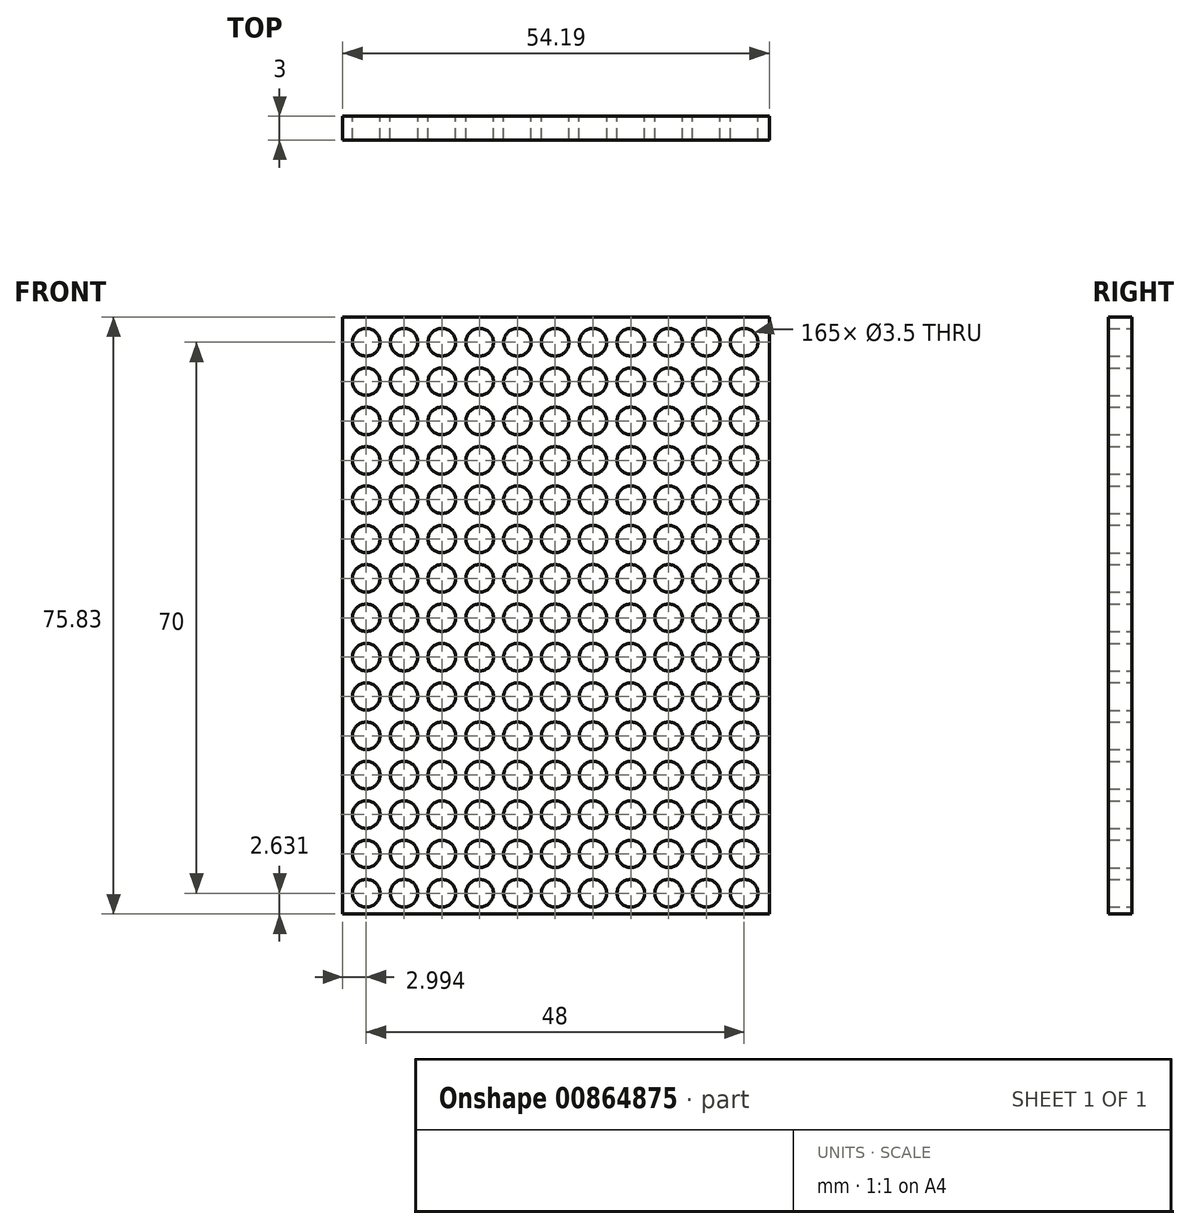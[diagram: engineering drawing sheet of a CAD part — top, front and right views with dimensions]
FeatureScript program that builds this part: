
annotation { "Feature Type Name" : "Feature", "Feature Type Description" : "" }
export const myFeature = defineFeature(function(context is Context, id is Id, definition is map)
    precondition{}
    {
        {
            var Q0;
            Q0=qCreatedBy(makeId("Front.planeOp"),FACE);
            var sketch = newSketch(context, id + "F0", { "sketchPlane" : qUnion([Q0])});
            skCircle(sketch, "E0", {"center": v(3, 2.63) * mm, "radius": 1.75 * mm});
            skCircle(sketch, "E1.0.1.0", {"center": v(3, 7.63) * mm, "radius": 1.75 * mm});
            skCircle(sketch, "E1.0.2.0", {"center": v(3, 12.63) * mm, "radius": 1.75 * mm});
            skCircle(sketch, "E1.0.3.0", {"center": v(3, 17.63) * mm, "radius": 1.75 * mm});
            skCircle(sketch, "E1.0.4.0", {"center": v(3, 22.63) * mm, "radius": 1.75 * mm});
            skCircle(sketch, "E1.0.5.0", {"center": v(3, 27.63) * mm, "radius": 1.75 * mm});
            skCircle(sketch, "E1.0.6.0", {"center": v(3, 32.63) * mm, "radius": 1.75 * mm});
            skCircle(sketch, "E1.0.7.0", {"center": v(3, 37.63) * mm, "radius": 1.75 * mm});
            skCircle(sketch, "E1.0.8.0", {"center": v(3, 42.63) * mm, "radius": 1.75 * mm});
            skCircle(sketch, "E1.0.9.0", {"center": v(3, 47.63) * mm, "radius": 1.75 * mm});
            skCircle(sketch, "E1.0.10.0", {"center": v(3, 52.63) * mm, "radius": 1.75 * mm});
            skCircle(sketch, "E1.0.11.0", {"center": v(3, 57.63) * mm, "radius": 1.75 * mm});
            skCircle(sketch, "E1.0.12.0", {"center": v(3, 62.63) * mm, "radius": 1.75 * mm});
            skCircle(sketch, "E1.0.13.0", {"center": v(3, 67.63) * mm, "radius": 1.75 * mm});
            skCircle(sketch, "E1.0.14.0", {"center": v(3, 72.63) * mm, "radius": 1.75 * mm});
            skCircle(sketch, "E1.1.0.0", {"center": v(7.8, 2.63) * mm, "radius": 1.75 * mm});
            skCircle(sketch, "E1.1.1.0", {"center": v(7.8, 7.63) * mm, "radius": 1.75 * mm});
            skCircle(sketch, "E1.1.2.0", {"center": v(7.8, 12.63) * mm, "radius": 1.75 * mm});
            skCircle(sketch, "E1.1.3.0", {"center": v(7.8, 17.63) * mm, "radius": 1.75 * mm});
            skCircle(sketch, "E1.1.4.0", {"center": v(7.8, 22.63) * mm, "radius": 1.75 * mm});
            skCircle(sketch, "E1.1.5.0", {"center": v(7.8, 27.63) * mm, "radius": 1.75 * mm});
            skCircle(sketch, "E1.1.6.0", {"center": v(7.8, 32.63) * mm, "radius": 1.75 * mm});
            skCircle(sketch, "E1.1.7.0", {"center": v(7.8, 37.63) * mm, "radius": 1.75 * mm});
            skCircle(sketch, "E1.1.8.0", {"center": v(7.8, 42.63) * mm, "radius": 1.75 * mm});
            skCircle(sketch, "E1.1.9.0", {"center": v(7.8, 47.63) * mm, "radius": 1.75 * mm});
            skCircle(sketch, "E1.1.10.0", {"center": v(7.8, 52.63) * mm, "radius": 1.75 * mm});
            skCircle(sketch, "E1.1.11.0", {"center": v(7.8, 57.63) * mm, "radius": 1.75 * mm});
            skCircle(sketch, "E1.1.12.0", {"center": v(7.8, 62.63) * mm, "radius": 1.75 * mm});
            skCircle(sketch, "E1.1.13.0", {"center": v(7.8, 67.63) * mm, "radius": 1.75 * mm});
            skCircle(sketch, "E1.1.14.0", {"center": v(7.8, 72.63) * mm, "radius": 1.75 * mm});
            skCircle(sketch, "E1.2.0.0", {"center": v(12.6, 2.63) * mm, "radius": 1.75 * mm});
            skCircle(sketch, "E1.2.1.0", {"center": v(12.6, 7.63) * mm, "radius": 1.75 * mm});
            skCircle(sketch, "E1.2.2.0", {"center": v(12.6, 12.63) * mm, "radius": 1.75 * mm});
            skCircle(sketch, "E1.2.3.0", {"center": v(12.6, 17.63) * mm, "radius": 1.75 * mm});
            skCircle(sketch, "E1.2.4.0", {"center": v(12.6, 22.63) * mm, "radius": 1.75 * mm});
            skCircle(sketch, "E1.2.5.0", {"center": v(12.6, 27.63) * mm, "radius": 1.75 * mm});
            skCircle(sketch, "E1.2.6.0", {"center": v(12.6, 32.63) * mm, "radius": 1.75 * mm});
            skCircle(sketch, "E1.2.7.0", {"center": v(12.6, 37.63) * mm, "radius": 1.75 * mm});
            skCircle(sketch, "E1.2.8.0", {"center": v(12.6, 42.63) * mm, "radius": 1.75 * mm});
            skCircle(sketch, "E1.2.9.0", {"center": v(12.6, 47.63) * mm, "radius": 1.75 * mm});
            skCircle(sketch, "E1.2.10.0", {"center": v(12.6, 52.63) * mm, "radius": 1.75 * mm});
            skCircle(sketch, "E1.2.11.0", {"center": v(12.6, 57.63) * mm, "radius": 1.75 * mm});
            skCircle(sketch, "E1.2.12.0", {"center": v(12.6, 62.63) * mm, "radius": 1.75 * mm});
            skCircle(sketch, "E1.2.13.0", {"center": v(12.6, 67.63) * mm, "radius": 1.75 * mm});
            skCircle(sketch, "E1.2.14.0", {"center": v(12.6, 72.63) * mm, "radius": 1.75 * mm});
            skCircle(sketch, "E1.3.0.0", {"center": v(17.4, 2.63) * mm, "radius": 1.75 * mm});
            skCircle(sketch, "E1.3.1.0", {"center": v(17.4, 7.63) * mm, "radius": 1.75 * mm});
            skCircle(sketch, "E1.3.2.0", {"center": v(17.4, 12.63) * mm, "radius": 1.75 * mm});
            skCircle(sketch, "E1.3.3.0", {"center": v(17.4, 17.63) * mm, "radius": 1.75 * mm});
            skCircle(sketch, "E1.3.4.0", {"center": v(17.4, 22.63) * mm, "radius": 1.75 * mm});
            skCircle(sketch, "E1.3.5.0", {"center": v(17.4, 27.63) * mm, "radius": 1.75 * mm});
            skCircle(sketch, "E1.3.6.0", {"center": v(17.4, 32.63) * mm, "radius": 1.75 * mm});
            skCircle(sketch, "E1.3.7.0", {"center": v(17.4, 37.63) * mm, "radius": 1.75 * mm});
            skCircle(sketch, "E1.3.8.0", {"center": v(17.4, 42.63) * mm, "radius": 1.75 * mm});
            skCircle(sketch, "E1.3.9.0", {"center": v(17.4, 47.63) * mm, "radius": 1.75 * mm});
            skCircle(sketch, "E1.3.10.0", {"center": v(17.4, 52.63) * mm, "radius": 1.75 * mm});
            skCircle(sketch, "E1.3.11.0", {"center": v(17.4, 57.63) * mm, "radius": 1.75 * mm});
            skCircle(sketch, "E1.3.12.0", {"center": v(17.4, 62.63) * mm, "radius": 1.75 * mm});
            skCircle(sketch, "E1.3.13.0", {"center": v(17.4, 67.63) * mm, "radius": 1.75 * mm});
            skCircle(sketch, "E1.3.14.0", {"center": v(17.4, 72.63) * mm, "radius": 1.75 * mm});
            skCircle(sketch, "E1.4.0.0", {"center": v(22.2, 2.63) * mm, "radius": 1.75 * mm});
            skCircle(sketch, "E1.4.1.0", {"center": v(22.2, 7.63) * mm, "radius": 1.75 * mm});
            skCircle(sketch, "E1.4.2.0", {"center": v(22.2, 12.63) * mm, "radius": 1.75 * mm});
            skCircle(sketch, "E1.4.3.0", {"center": v(22.2, 17.63) * mm, "radius": 1.75 * mm});
            skCircle(sketch, "E1.4.4.0", {"center": v(22.2, 22.63) * mm, "radius": 1.75 * mm});
            skCircle(sketch, "E1.4.5.0", {"center": v(22.2, 27.63) * mm, "radius": 1.75 * mm});
            skCircle(sketch, "E1.4.6.0", {"center": v(22.2, 32.63) * mm, "radius": 1.75 * mm});
            skCircle(sketch, "E1.4.7.0", {"center": v(22.2, 37.63) * mm, "radius": 1.75 * mm});
            skCircle(sketch, "E1.4.8.0", {"center": v(22.2, 42.63) * mm, "radius": 1.75 * mm});
            skCircle(sketch, "E1.4.9.0", {"center": v(22.2, 47.63) * mm, "radius": 1.75 * mm});
            skCircle(sketch, "E1.4.10.0", {"center": v(22.2, 52.63) * mm, "radius": 1.75 * mm});
            skCircle(sketch, "E1.4.11.0", {"center": v(22.2, 57.63) * mm, "radius": 1.75 * mm});
            skCircle(sketch, "E1.4.12.0", {"center": v(22.2, 62.63) * mm, "radius": 1.75 * mm});
            skCircle(sketch, "E1.4.13.0", {"center": v(22.2, 67.63) * mm, "radius": 1.75 * mm});
            skCircle(sketch, "E1.4.14.0", {"center": v(22.2, 72.63) * mm, "radius": 1.75 * mm});
            skCircle(sketch, "E1.5.0.0", {"center": v(27, 2.63) * mm, "radius": 1.75 * mm});
            skCircle(sketch, "E1.5.1.0", {"center": v(27, 7.63) * mm, "radius": 1.75 * mm});
            skCircle(sketch, "E1.5.2.0", {"center": v(27, 12.63) * mm, "radius": 1.75 * mm});
            skCircle(sketch, "E1.5.3.0", {"center": v(27, 17.63) * mm, "radius": 1.75 * mm});
            skCircle(sketch, "E1.5.4.0", {"center": v(27, 22.63) * mm, "radius": 1.75 * mm});
            skCircle(sketch, "E1.5.5.0", {"center": v(27, 27.63) * mm, "radius": 1.75 * mm});
            skCircle(sketch, "E1.5.6.0", {"center": v(27, 32.63) * mm, "radius": 1.75 * mm});
            skCircle(sketch, "E1.5.7.0", {"center": v(27, 37.63) * mm, "radius": 1.75 * mm});
            skCircle(sketch, "E1.5.8.0", {"center": v(27, 42.63) * mm, "radius": 1.75 * mm});
            skCircle(sketch, "E1.5.9.0", {"center": v(27, 47.63) * mm, "radius": 1.75 * mm});
            skCircle(sketch, "E1.5.10.0", {"center": v(27, 52.63) * mm, "radius": 1.75 * mm});
            skCircle(sketch, "E1.5.11.0", {"center": v(27, 57.63) * mm, "radius": 1.75 * mm});
            skCircle(sketch, "E1.5.12.0", {"center": v(27, 62.63) * mm, "radius": 1.75 * mm});
            skCircle(sketch, "E1.5.13.0", {"center": v(27, 67.63) * mm, "radius": 1.75 * mm});
            skCircle(sketch, "E1.5.14.0", {"center": v(27, 72.63) * mm, "radius": 1.75 * mm});
            skCircle(sketch, "E1.6.0.0", {"center": v(31.8, 2.63) * mm, "radius": 1.75 * mm});
            skCircle(sketch, "E1.6.1.0", {"center": v(31.8, 7.63) * mm, "radius": 1.75 * mm});
            skCircle(sketch, "E1.6.2.0", {"center": v(31.8, 12.63) * mm, "radius": 1.75 * mm});
            skCircle(sketch, "E1.6.3.0", {"center": v(31.8, 17.63) * mm, "radius": 1.75 * mm});
            skCircle(sketch, "E1.6.4.0", {"center": v(31.8, 22.63) * mm, "radius": 1.75 * mm});
            skCircle(sketch, "E1.6.5.0", {"center": v(31.8, 27.63) * mm, "radius": 1.75 * mm});
            skCircle(sketch, "E1.6.6.0", {"center": v(31.8, 32.63) * mm, "radius": 1.75 * mm});
            skCircle(sketch, "E1.6.7.0", {"center": v(31.8, 37.63) * mm, "radius": 1.75 * mm});
            skCircle(sketch, "E1.6.8.0", {"center": v(31.8, 42.63) * mm, "radius": 1.75 * mm});
            skCircle(sketch, "E1.6.9.0", {"center": v(31.8, 47.63) * mm, "radius": 1.75 * mm});
            skCircle(sketch, "E1.6.10.0", {"center": v(31.8, 52.63) * mm, "radius": 1.75 * mm});
            skCircle(sketch, "E1.6.11.0", {"center": v(31.8, 57.63) * mm, "radius": 1.75 * mm});
            skCircle(sketch, "E1.6.12.0", {"center": v(31.8, 62.63) * mm, "radius": 1.75 * mm});
            skCircle(sketch, "E1.6.13.0", {"center": v(31.8, 67.63) * mm, "radius": 1.75 * mm});
            skCircle(sketch, "E1.6.14.0", {"center": v(31.8, 72.63) * mm, "radius": 1.75 * mm});
            skCircle(sketch, "E1.7.0.0", {"center": v(36.6, 2.63) * mm, "radius": 1.75 * mm});
            skCircle(sketch, "E1.7.1.0", {"center": v(36.6, 7.63) * mm, "radius": 1.75 * mm});
            skCircle(sketch, "E1.7.2.0", {"center": v(36.6, 12.63) * mm, "radius": 1.75 * mm});
            skCircle(sketch, "E1.7.3.0", {"center": v(36.6, 17.63) * mm, "radius": 1.75 * mm});
            skCircle(sketch, "E1.7.4.0", {"center": v(36.6, 22.63) * mm, "radius": 1.75 * mm});
            skCircle(sketch, "E1.7.5.0", {"center": v(36.6, 27.63) * mm, "radius": 1.75 * mm});
            skCircle(sketch, "E1.7.6.0", {"center": v(36.6, 32.63) * mm, "radius": 1.75 * mm});
            skCircle(sketch, "E1.7.7.0", {"center": v(36.6, 37.63) * mm, "radius": 1.75 * mm});
            skCircle(sketch, "E1.7.8.0", {"center": v(36.6, 42.63) * mm, "radius": 1.75 * mm});
            skCircle(sketch, "E1.7.9.0", {"center": v(36.6, 47.63) * mm, "radius": 1.75 * mm});
            skCircle(sketch, "E1.7.10.0", {"center": v(36.6, 52.63) * mm, "radius": 1.75 * mm});
            skCircle(sketch, "E1.7.11.0", {"center": v(36.6, 57.63) * mm, "radius": 1.75 * mm});
            skCircle(sketch, "E1.7.12.0", {"center": v(36.6, 62.63) * mm, "radius": 1.75 * mm});
            skCircle(sketch, "E1.7.13.0", {"center": v(36.6, 67.63) * mm, "radius": 1.75 * mm});
            skCircle(sketch, "E1.7.14.0", {"center": v(36.6, 72.63) * mm, "radius": 1.75 * mm});
            skCircle(sketch, "E1.8.0.0", {"center": v(41.4, 2.63) * mm, "radius": 1.75 * mm});
            skCircle(sketch, "E1.8.1.0", {"center": v(41.4, 7.63) * mm, "radius": 1.75 * mm});
            skCircle(sketch, "E1.8.2.0", {"center": v(41.4, 12.63) * mm, "radius": 1.75 * mm});
            skCircle(sketch, "E1.8.3.0", {"center": v(41.4, 17.63) * mm, "radius": 1.75 * mm});
            skCircle(sketch, "E1.8.4.0", {"center": v(41.4, 22.63) * mm, "radius": 1.75 * mm});
            skCircle(sketch, "E1.8.5.0", {"center": v(41.4, 27.63) * mm, "radius": 1.75 * mm});
            skCircle(sketch, "E1.8.6.0", {"center": v(41.4, 32.63) * mm, "radius": 1.75 * mm});
            skCircle(sketch, "E1.8.7.0", {"center": v(41.4, 37.63) * mm, "radius": 1.75 * mm});
            skCircle(sketch, "E1.8.8.0", {"center": v(41.4, 42.63) * mm, "radius": 1.75 * mm});
            skCircle(sketch, "E1.8.9.0", {"center": v(41.4, 47.63) * mm, "radius": 1.75 * mm});
            skCircle(sketch, "E1.8.10.0", {"center": v(41.4, 52.63) * mm, "radius": 1.75 * mm});
            skCircle(sketch, "E1.8.11.0", {"center": v(41.4, 57.63) * mm, "radius": 1.75 * mm});
            skCircle(sketch, "E1.8.12.0", {"center": v(41.4, 62.63) * mm, "radius": 1.75 * mm});
            skCircle(sketch, "E1.8.13.0", {"center": v(41.4, 67.63) * mm, "radius": 1.75 * mm});
            skCircle(sketch, "E1.8.14.0", {"center": v(41.4, 72.63) * mm, "radius": 1.75 * mm});
            skCircle(sketch, "E1.9.0.0", {"center": v(46.2, 2.63) * mm, "radius": 1.75 * mm});
            skCircle(sketch, "E1.9.1.0", {"center": v(46.2, 7.63) * mm, "radius": 1.75 * mm});
            skCircle(sketch, "E1.9.2.0", {"center": v(46.2, 12.63) * mm, "radius": 1.75 * mm});
            skCircle(sketch, "E1.9.3.0", {"center": v(46.2, 17.63) * mm, "radius": 1.75 * mm});
            skCircle(sketch, "E1.9.4.0", {"center": v(46.2, 22.63) * mm, "radius": 1.75 * mm});
            skCircle(sketch, "E1.9.5.0", {"center": v(46.2, 27.63) * mm, "radius": 1.75 * mm});
            skCircle(sketch, "E1.9.6.0", {"center": v(46.2, 32.63) * mm, "radius": 1.75 * mm});
            skCircle(sketch, "E1.9.7.0", {"center": v(46.2, 37.63) * mm, "radius": 1.75 * mm});
            skCircle(sketch, "E1.9.8.0", {"center": v(46.2, 42.63) * mm, "radius": 1.75 * mm});
            skCircle(sketch, "E1.9.9.0", {"center": v(46.2, 47.63) * mm, "radius": 1.75 * mm});
            skCircle(sketch, "E1.9.10.0", {"center": v(46.2, 52.63) * mm, "radius": 1.75 * mm});
            skCircle(sketch, "E1.9.11.0", {"center": v(46.2, 57.63) * mm, "radius": 1.75 * mm});
            skCircle(sketch, "E1.9.12.0", {"center": v(46.2, 62.63) * mm, "radius": 1.75 * mm});
            skCircle(sketch, "E1.9.13.0", {"center": v(46.2, 67.63) * mm, "radius": 1.75 * mm});
            skCircle(sketch, "E1.9.14.0", {"center": v(46.2, 72.63) * mm, "radius": 1.75 * mm});
            skCircle(sketch, "E1.10.0.0", {"center": v(51, 2.63) * mm, "radius": 1.75 * mm});
            skCircle(sketch, "E1.10.1.0", {"center": v(51, 7.63) * mm, "radius": 1.75 * mm});
            skCircle(sketch, "E1.10.2.0", {"center": v(51, 12.63) * mm, "radius": 1.75 * mm});
            skCircle(sketch, "E1.10.3.0", {"center": v(51, 17.63) * mm, "radius": 1.75 * mm});
            skCircle(sketch, "E1.10.4.0", {"center": v(51, 22.63) * mm, "radius": 1.75 * mm});
            skCircle(sketch, "E1.10.5.0", {"center": v(51, 27.63) * mm, "radius": 1.75 * mm});
            skCircle(sketch, "E1.10.6.0", {"center": v(51, 32.63) * mm, "radius": 1.75 * mm});
            skCircle(sketch, "E1.10.7.0", {"center": v(51, 37.63) * mm, "radius": 1.75 * mm});
            skCircle(sketch, "E1.10.8.0", {"center": v(51, 42.63) * mm, "radius": 1.75 * mm});
            skCircle(sketch, "E1.10.9.0", {"center": v(51, 47.63) * mm, "radius": 1.75 * mm});
            skCircle(sketch, "E1.10.10.0", {"center": v(51, 52.63) * mm, "radius": 1.75 * mm});
            skCircle(sketch, "E1.10.11.0", {"center": v(51, 57.63) * mm, "radius": 1.75 * mm});
            skCircle(sketch, "E1.10.12.0", {"center": v(51, 62.63) * mm, "radius": 1.75 * mm});
            skCircle(sketch, "E1.10.13.0", {"center": v(51, 67.63) * mm, "radius": 1.75 * mm});
            skCircle(sketch, "E1.10.14.0", {"center": v(51, 72.63) * mm, "radius": 1.75 * mm});
            skLineSegment(sketch, "E1.direction1", {"start": v(3, 2.63) * mm, "end": v(7.8, 2.63) * mm, "construction": true});
            skLineSegment(sketch, "E1.direction2", {"start": v(3, 2.63) * mm, "end": v(3, 7.63) * mm, "construction": true});
            skLineSegment(sketch, "E2.bottom", {"start": v(0, 0) * mm, "end": v(54.2, 0) * mm});
            skLineSegment(sketch, "E2.top", {"start": v(0, 75.83) * mm, "end": v(54.2, 75.83) * mm});
            skLineSegment(sketch, "E2.left", {"start": v(0, 0) * mm, "end": v(0, 75.83) * mm});
            skLineSegment(sketch, "E2.right", {"start": v(54.2, 0) * mm, "end": v(54.2, 75.83) * mm});
            skSolve(sketch);
        }
        {
            var Q0;
            Q0 = qSketchRegion(id + "F0", true);
            extrude(context, id + "F1", {"entities" : qUnion([Q0]), "depth" : 3 * mm, "offsetDistance" : 25 * mm});
        }
    });
